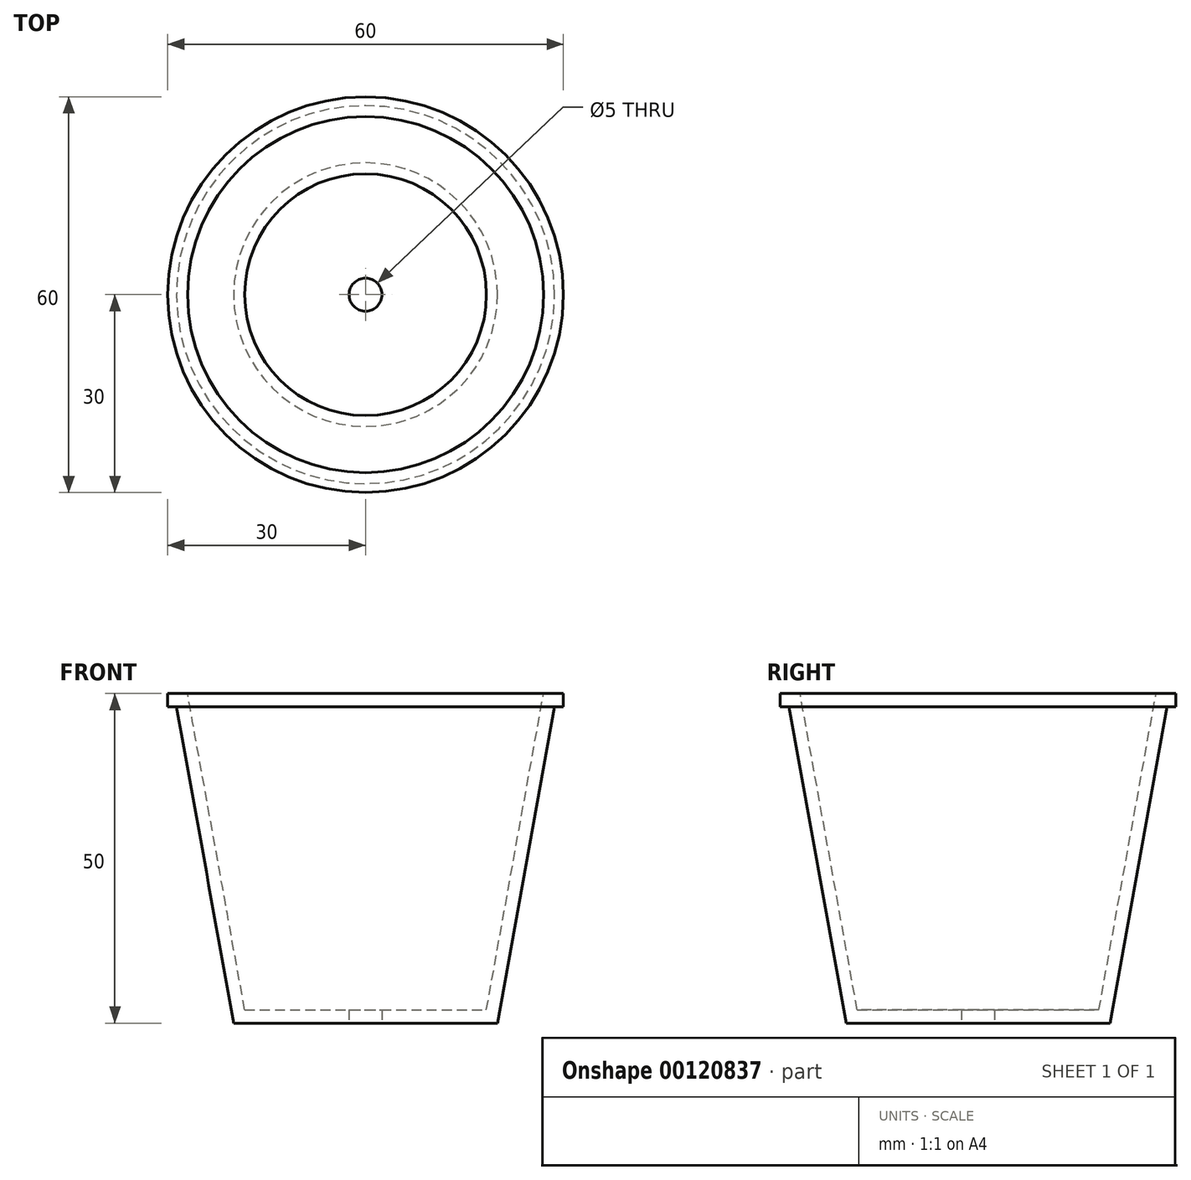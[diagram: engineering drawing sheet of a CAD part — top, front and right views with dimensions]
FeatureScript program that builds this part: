
annotation { "Feature Type Name" : "Feature", "Feature Type Description" : "" }
export const myFeature = defineFeature(function(context is Context, id is Id, definition is map)
    precondition{}
    {
        {
            var Q0;
            Q0=qCreatedBy(makeId("Front.planeOp"),FACE);
            var sketch = newSketch(context, id + "F0", { "sketchPlane" : qUnion([Q0])});
            skLineSegment(sketch, "E0", {"start": v(2.5, 2) * mm, "end": v(2.5, 0) * mm});
            skLineSegment(sketch, "E1", {"start": v(2.5, 0) * mm, "end": v(20, 0) * mm});
            skLineSegment(sketch, "E2", {"start": v(20, 0) * mm, "end": v(28.67, 48) * mm});
            skLineSegment(sketch, "E3", {"start": v(28.67, 48) * mm, "end": v(30, 48) * mm});
            skLineSegment(sketch, "E4", {"start": v(30, 48) * mm, "end": v(30, 50) * mm});
            skLineSegment(sketch, "E5", {"start": v(30, 50) * mm, "end": v(27, 50) * mm});
            skLineSegment(sketch, "E6", {"start": v(27, 50) * mm, "end": v(18.33, 2) * mm});
            skLineSegment(sketch, "E7", {"start": v(18.33, 2) * mm, "end": v(2.5, 2) * mm});
            skLineSegment(sketch, "E8", {"start": v(0, 0) * mm, "end": v(0, 51.76) * mm, "construction": true});
            skSolve(sketch);
        }
        {
            var Q0;
            Q0=makeQuery(id+"F0.imprint","IMPRINT",FACE,{"disambiguationData":[TD([[makeQuery(id+"F0.imprint","IMPRINT",EDGE,{"derivedFrom":sQuery(id+"F0.wireOp",EDGE,"E0")}),1.0]])]});
            var Q1;
            Q1=sQuery(id+"F0.wireOp",EDGE,"E6");
            var Q2;
            Q2=sQuery(id+"F0.wireOp",EDGE,"E5");
            var Q3;
            Q3=sQuery(id+"F0.wireOp",EDGE,"E4");
            var Q4;
            Q4=sQuery(id+"F0.wireOp",EDGE,"E3");
            var Q5;
            Q5=sQuery(id+"F0.wireOp",EDGE,"E2");
            var Q6;
            Q6=sQuery(id+"F0.wireOp",EDGE,"E1");
            var Q7;
            Q7=sQuery(id+"F0.wireOp",EDGE,"E7");
            var Q8;
            Q8=sQuery(id+"F0.wireOp",EDGE,"E0");
            var Q9;
            Q9=sQuery(id+"F0.wireOp",EDGE,"E8");
            revolve(context, id + "F1", {"entities" : qUnion([Q0]), "surfaceEntities" : qUnion([Q1, Q2, Q3, Q4, Q5, Q6, Q7, Q8]), "axis" : qUnion([Q9]), "revolveType" : RevolveType.FULL});
        }
    });
